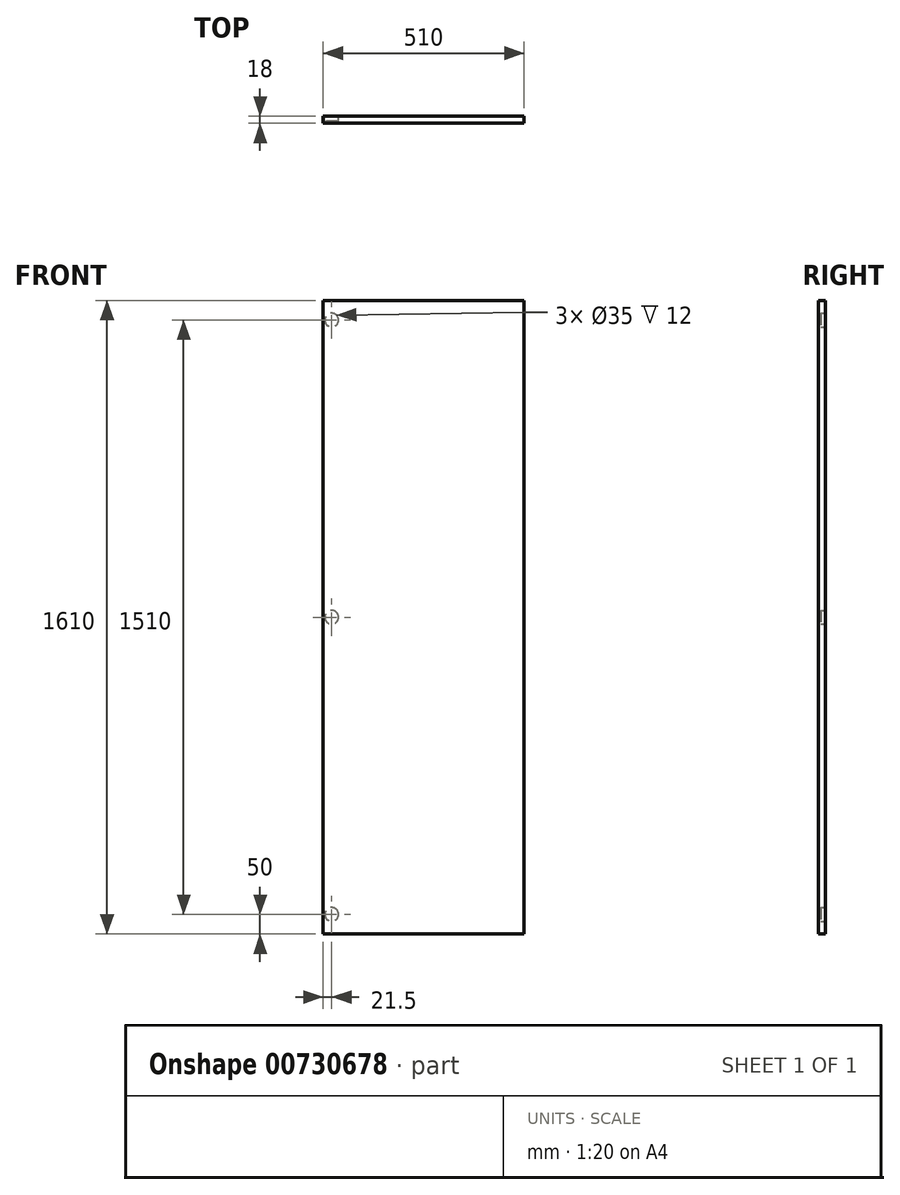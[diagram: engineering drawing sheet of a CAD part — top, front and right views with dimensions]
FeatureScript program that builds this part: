
annotation { "Feature Type Name" : "Feature", "Feature Type Description" : "" }
export const myFeature = defineFeature(function(context is Context, id is Id, definition is map)
    precondition{}
    {
        {
            var Q0;
            Q0=qCreatedBy(makeId("Front.planeOp"),FACE);
            var sketch = newSketch(context, id + "F0", { "sketchPlane" : qUnion([Q0])});
            skLineSegment(sketch, "E0.bottom", {"start": v(-255, 805) * mm, "end": v(255, 805) * mm});
            skLineSegment(sketch, "E0.top", {"start": v(-255, -805) * mm, "end": v(255, -805) * mm});
            skLineSegment(sketch, "E0.left", {"start": v(-255, 805) * mm, "end": v(-255, -805) * mm});
            skLineSegment(sketch, "E0.right", {"start": v(255, 805) * mm, "end": v(255, -805) * mm});
            skPoint(sketch, "E0.middle", {"position": v(0, 0) * mm});
            skSolve(sketch);
        }
        {
            var Q0;
            Q0 = qSketchRegion(id + "F0", true);
            extrude(context, id + "F1", {"entities" : qUnion([Q0]), "depth" : 18 * mm, "offsetDistance" : 25 * mm});
        }
        {
            var Q0;
            Q0=makeQuery(id+"F1.opExtrude","CAP_FACE",FACE,{"disambiguationData":[OSD([sQuery(id+"F0.wireOp",EDGE,"E0.bottom"),sQuery(id+"F0.wireOp",EDGE,"E0.top"),sQuery(id+"F0.wireOp",EDGE,"E0.left"),sQuery(id+"F0.wireOp",EDGE,"E0.right")])],"isStart":true});
            var sketch = newSketch(context, id + "F2", { "sketchPlane" : qUnion([Q0])});
            skCircle(sketch, "E1", {"center": v(233.5, -755) * mm, "radius": 17.5 * mm});
            skLineSegment(sketch, "E2", {"start": v(233.5, -755) * mm, "end": v(233.5, -805) * mm, "construction": true});
            skCircle(sketch, "E3.0.1.0", {"center": v(233.5, 0) * mm, "radius": 17.5 * mm});
            skCircle(sketch, "E3.0.2.0", {"center": v(233.5, 755) * mm, "radius": 17.5 * mm});
            skLineSegment(sketch, "E3.direction1", {"start": v(233.5, -755) * mm, "end": v(237.32, -755) * mm, "construction": true});
            skLineSegment(sketch, "E3.direction2", {"start": v(233.5, -755) * mm, "end": v(233.5, 0) * mm, "construction": true});
            skSolve(sketch);
        }
        {
            var Q0;
            Q0 = qSketchRegion(id + "F2", true);
            extrude(context, id + "F3", {"entities" : qUnion([Q0]), "operationType" : NewBodyOperationType.REMOVE, "oppositeDirection" : true, "depth" : 12 * mm, "offsetDistance" : 25 * mm});
        }
    });
